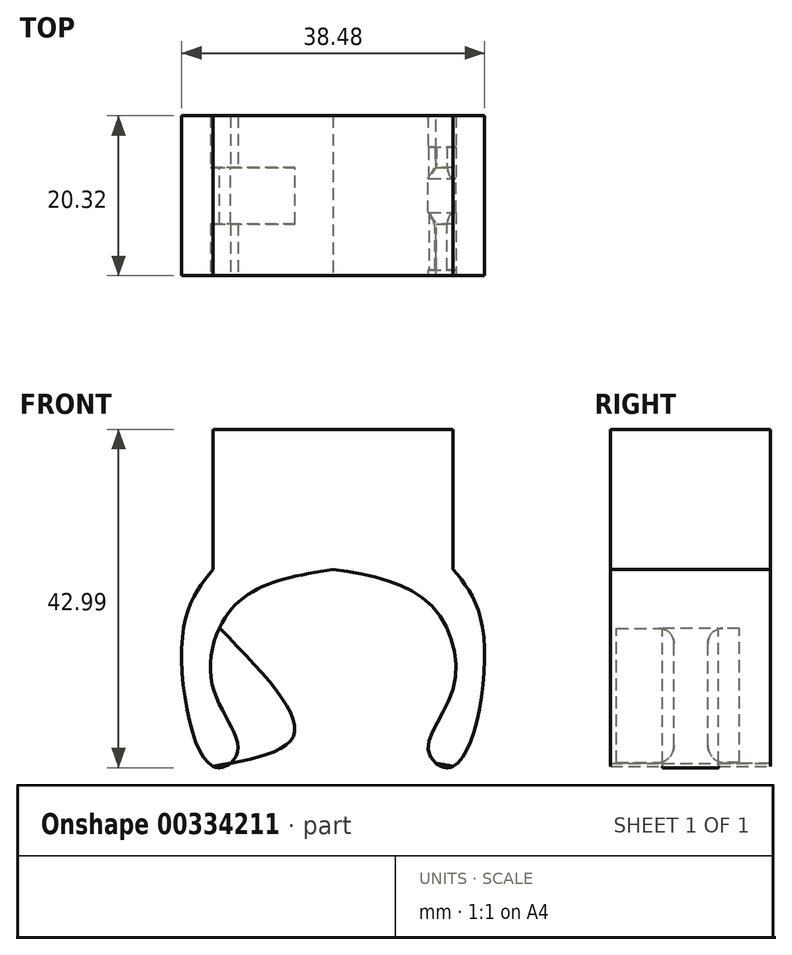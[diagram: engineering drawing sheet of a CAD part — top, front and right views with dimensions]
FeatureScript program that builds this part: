
annotation { "Feature Type Name" : "Feature", "Feature Type Description" : "" }
export const myFeature = defineFeature(function(context is Context, id is Id, definition is map)
    precondition{}
    {
        {
            var Q0;
            Q0=qCreatedBy(makeId("Front.planeOp"),FACE);
            var sketch = newSketch(context, id + "F0", { "sketchPlane" : qUnion([Q0])});
            skLineSegment(sketch, "E0", {"start": v(-59.04, 44.52) * mm, "end": v(-28.56, 44.52) * mm});
            skLineSegment(sketch, "E1", {"start": v(-59.04, 44.52) * mm, "end": v(-59.04, 26.74) * mm});
            skLineSegment(sketch, "E2", {"start": v(-28.56, 44.52) * mm, "end": v(-28.56, 26.74) * mm});
            skFitSpline(sketch, "E3", {"points": [v(-59.04, 26.74) * mm, v(-62.9, 18.45) * mm, v(-59.04, 1.7) * mm, v(-55.91, 3.66) * mm, v(-59.04, 11.62) * mm, v(-56.08, 22.35) * mm, v(-43.8, 26.74) * mm], "startDerivative": vector(-31.9, -38.73) * mm, "endDerivative": vector(73.46, 12.07) * mm});
            skFitSpline(sketch, "E4.MirrorCS", {"points": [v(-28.56, 26.74) * mm, v(-24.7, 18.45) * mm, v(-28.56, 1.7) * mm, v(-31.7, 3.66) * mm, v(-28.56, 11.62) * mm, v(-31.53, 22.35) * mm, v(-43.8, 26.74) * mm], "startDerivative": vector(31.9, -38.73) * mm, "endDerivative": vector(-73.46, 12.07) * mm});
            skFitSpline(sketch, "E5", {"points": [v(-59.04, 1.7) * mm, v(-48.76, 5.77) * mm, v(-58.25, 19.28) * mm], "startDerivative": vector(31.86, 5.53) * mm, "endDerivative": vector(-28.26, 28.83) * mm});
            skFitSpline(sketch, "E6.MirrorCS", {"points": [v(-28.56, 1.7) * mm, v(-38.85, 5.77) * mm, v(-29.36, 19.28) * mm], "startDerivative": vector(-31.86, 5.53) * mm, "endDerivative": vector(28.26, 28.83) * mm});
            skLineSegment(sketch, "E7", {"start": v(-11.74, 44.82) * mm, "end": v(-11.74, 10.62) * mm});
            skSolve(sketch);
        }
        {
            var Q0;
            Q0=makeQuery(id+"F0.imprint","IMPRINT",FACE,{"disambiguationData":[TD([[makeQuery(id+"F0.imprint","IMPRINT",EDGE,{"derivedFrom":sQuery(id+"F0.wireOp",EDGE,"E0")}),-1.0]])]});
            extrude(context, id + "F1", {"entities" : qUnion([Q0]), "depth" : 10.16 * mm, "hasSecondDirection" : true, "secondDirectionOppositeDirection" : true, "secondDirectionDepth" : 10.16 * mm});
        }
        {
            var Q0;
            Q0 = qSketchRegion(id + "F0", true);
            extrude(context, id + "F2", {"entities" : qUnion([Q0]), "operationType" : NewBodyOperationType.ADD, "oppositeDirection" : true, "depth" : 3.56 * mm, "hasSecondDirection" : true, "secondDirectionOppositeDirection" : false, "secondDirectionDepth" : 3.56 * mm});
        }
        {
            var Q0;
            Q0=makeQuery(id+"F1.opExtrude","SWEPT_BODY",BODY,{"disambiguationData":[OSD([sQuery(id+"F0.wireOp",EDGE,"E0"),sQuery(id+"F0.wireOp",EDGE,"E1"),sQuery(id+"F0.wireOp",EDGE,"E2"),sQuery(id+"F0.wireOp",EDGE,"E3"),sQuery(id+"F0.wireOp",EDGE,"E4.MirrorCS"),sQuery(id+"F0.wireOp",EDGE,"E5"),sQuery(id+"F0.wireOp",EDGE,"E6.MirrorCS")])]});
            var Q1;
            Q1=qCreatedBy(makeId("Front.planeOp"),FACE);
            mirror(context, id + "F3", {"entities" : qUnion([Q0]), "mirrorPlane" : qUnion([Q1])});
        }
        {
            var Q0;
            Q0=qCreatedBy(makeId("Front.planeOp"),FACE);
            var sketch = newSketch(context, id + "F4", { "sketchPlane" : qUnion([Q0])});
            skFitSpline(sketch, "E8.MirrorCS", {"points": [v(-59.17, 1.76) * mm, v(-48.88, 5.74) * mm, v(-58.33, 19.34) * mm], "startDerivative": vector(31.78, 6.02) * mm, "endDerivative": vector(-28.24, 28.85) * mm});
            skFitSpline(sketch, "E9.MirrorCS", {"points": [v(-28.5, 1.76) * mm, v(-38.8, 5.74) * mm, v(-29.32, 19.25) * mm], "startDerivative": vector(-31.8, 5.85) * mm, "endDerivative": vector(28.25, 28.84) * mm});
            skFitSpline(sketch, "E10.MirrorCS", {"points": [v(-59.18, 26.7) * mm, v(-63.03, 18.42) * mm, v(-59.16, 1.75) * mm, v(-56.1, 3.67) * mm, v(-59.18, 11.59) * mm, v(-56.21, 22.32) * mm, v(-43.93, 26.7) * mm], "startDerivative": vector(-31.9, -38.73) * mm, "endDerivative": vector(73.46, 12.07) * mm});
            skFitSpline(sketch, "E11.MirrorCS", {"points": [v(-28.46, 26.71) * mm, v(-24.66, 18.41) * mm, v(-28.5, 1.74) * mm, v(-31.57, 3.68) * mm, v(-28.52, 11.58) * mm, v(-31.48, 22.31) * mm, v(-43.76, 26.7) * mm], "startDerivative": vector(32.08, -38.58) * mm, "endDerivative": vector(-73.46, 12.08) * mm});
            skSolve(sketch);
        }
        {
            var Q0;
            Q0 = qSketchRegion(id + "F4", true);
            extrude(context, id + "F5", {"entities" : qUnion([Q0]), "operationType" : NewBodyOperationType.REMOVE, "depth" : 9.4 * mm, "hasSecondDirection" : true, "secondDirectionOppositeDirection" : false, "secondDirectionDepth" : 2.1 * mm});
        }
        {
            var Q0;
            Q0 = qSketchRegion(id + "F4", true);
            extrude(context, id + "F6", {"entities" : qUnion([Q0]), "operationType" : NewBodyOperationType.REMOVE, "oppositeDirection" : true, "depth" : 6.2 * mm, "hasSecondDirection" : true, "secondDirectionOppositeDirection" : true, "secondDirectionDepth" : 2.2 * mm});
        }
        {
            var Q0;
            Q0=makeQuery(id+"F5.boolean.opBoolean","COPY",EDGE,{"disambiguationData":[OD(1.0)],"derivedFrom":makeQuery(id+"F5.opExtrude","CAP_EDGE",EDGE,{"disambiguationData":[OSD([sQuery(id+"F4.wireOp",EDGE,"E8.MirrorCS")])],"isStart":true})});
            var Q1;
            Q1=makeQuery(id+"F5.boolean.opBoolean","COPY",EDGE,{"disambiguationData":[OD(1.0)],"derivedFrom":makeQuery(id+"F5.opExtrude","CAP_EDGE",EDGE,{"disambiguationData":[OSD([sQuery(id+"F4.wireOp",EDGE,"E9.MirrorCS")])],"isStart":true})});
            var Q2;
            Q2=makeQuery(id+"F6.boolean.opBoolean","COPY",EDGE,{"disambiguationData":[OD(1.0)],"derivedFrom":makeQuery(id+"F6.opExtrude","CAP_EDGE",EDGE,{"disambiguationData":[OSD([sQuery(id+"F4.wireOp",EDGE,"E8.MirrorCS")])],"isStart":true})});
            var Q3;
            Q3=makeQuery(id+"F6.boolean.opBoolean","COPY",EDGE,{"disambiguationData":[OD(1.0)],"derivedFrom":makeQuery(id+"F6.opExtrude","CAP_EDGE",EDGE,{"disambiguationData":[OSD([sQuery(id+"F4.wireOp",EDGE,"E9.MirrorCS")])],"isStart":true})});
            fillet(context, id + "F7", {"entities" : qUnion([Q0, Q1, Q2, Q3]), "radius" : 1.93 * mm, "allowEdgeOverflow" : false});
        }
    });
